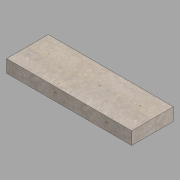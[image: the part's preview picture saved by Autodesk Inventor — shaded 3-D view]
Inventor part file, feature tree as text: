
AUTODESK INVENTOR PART (.ipt)
format: ipt  version: 2022 (Build 260153000, 153)  size: 114,176 bytes
history: native  units: in
note: dims shown in document units (in); Inventor stores cm internally (conversion verified against a paired STEP export)
features: extrude x1, sketch x1
ambient origin geometry x8: Origin, YZ Plane, XZ Plane, XY Plane, X Axis, Y Axis, Z Axis, Center Point
bodies: Solid1 (feature_tree)
feature tree (2):
  extrude  "Extrusion1"  Depth=18.0in
  sketch  "Sketch1"  dims[d0=54.0in d1=18.0in d2=5.5in d3=0.0in]
